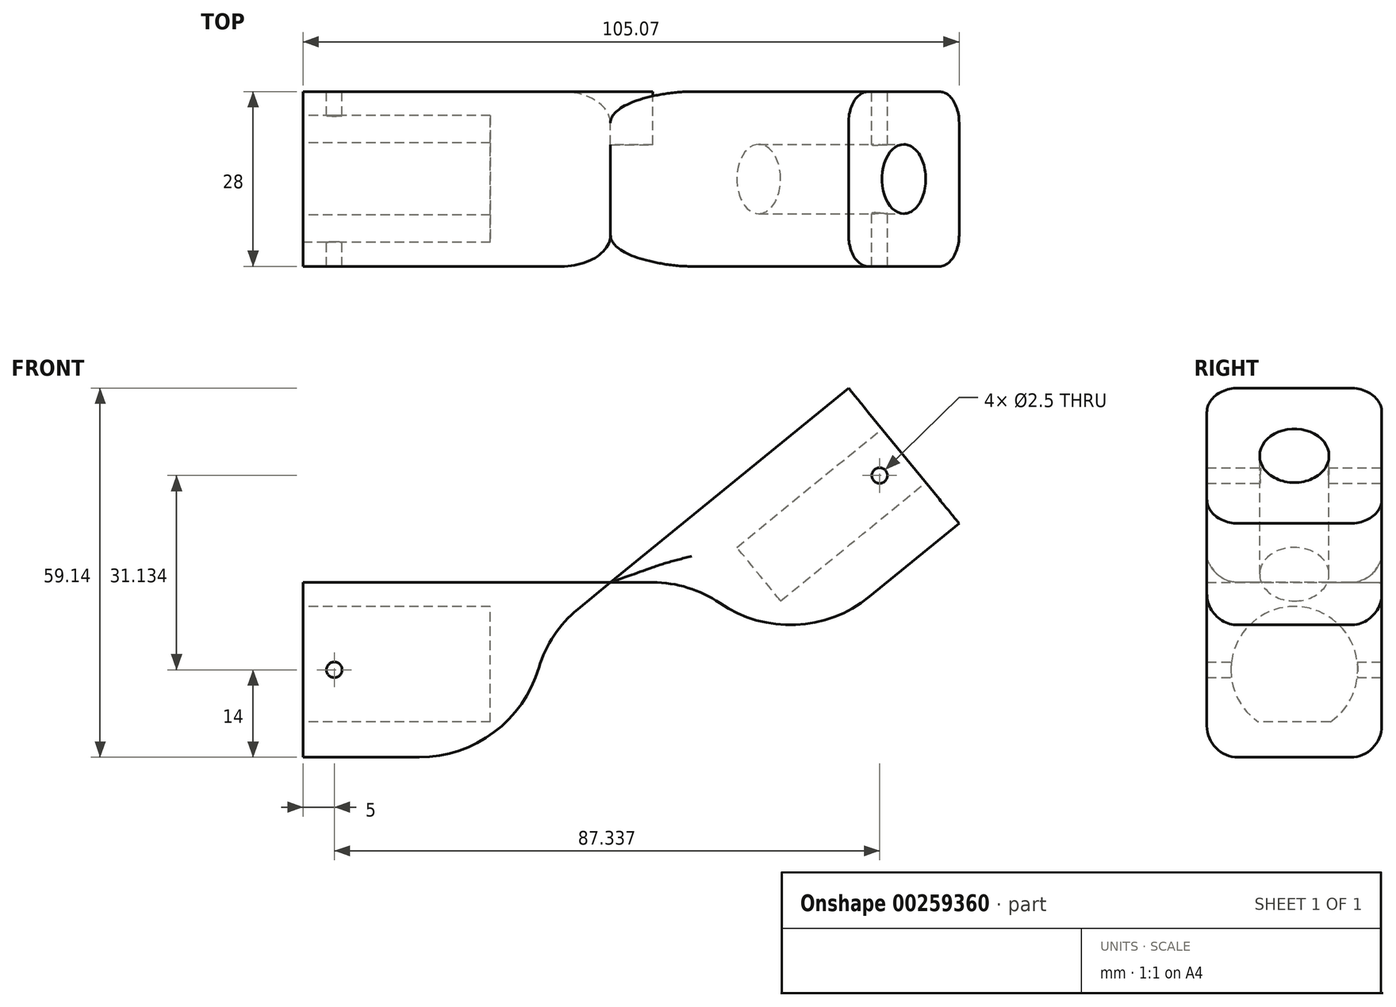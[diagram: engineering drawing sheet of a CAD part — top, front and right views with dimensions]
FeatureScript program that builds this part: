
annotation { "Feature Type Name" : "Feature", "Feature Type Description" : "" }
export const myFeature = defineFeature(function(context is Context, id is Id, definition is map)
    precondition{}
    {
        {
            var Q0;
            Q0=qCreatedBy(makeId("Front.planeOp"),FACE);
            var sketch = newSketch(context, id + "F0", { "sketchPlane" : qUnion([Q0])});
            skLineSegment(sketch, "E0.bottom", {"start": v(-75, 28) * mm, "end": v(-19, 28) * mm});
            skLineSegment(sketch, "E0.top", {"start": v(-75, 0) * mm, "end": v(-35.73, 0) * mm});
            skLineSegment(sketch, "E0.left", {"start": v(-75, 28) * mm, "end": v(-75, 0) * mm});
            skCircle(sketch, "E1", {"center": v(-19, 9) * mm, "radius": 19 * mm});
            skPoint(sketch, "E2.orphan", {"position": v(0, 0) * mm});
            skSolve(sketch);
        }
        {
            var Q0;
            Q0 = qSketchRegion(id + "F0", true);
            extrude(context, id + "F1", {"entities" : qUnion([Q0]), "endBound" : BoundingType.SYMMETRIC, "depth" : 28 * mm});
        }
        {
            var Q0;
            Q0=qCreatedBy(makeId("Front.planeOp"),FACE);
            var sketch = newSketch(context, id + "F2", { "sketchPlane" : qUnion([Q0])});
            skArc(sketch, "E3", {"start": v(-31.02, 23.72) * mm, "mid": v(-25.47, -8.87) * mm, "end": v(-0.35, 12.61) * mm});
            skLineSegment(sketch, "E4", {"start": v(-0.35, 12.61) * mm, "end": v(30.07, 37.45) * mm});
            skLineSegment(sketch, "E5", {"start": v(30.07, 37.45) * mm, "end": v(12.35, 59.14) * mm});
            skLineSegment(sketch, "E6", {"start": v(12.35, 59.14) * mm, "end": v(-31.02, 23.72) * mm});
            skSolve(sketch);
        }
        {
            var Q0;
            Q0 = qSketchRegion(id + "F2", true);
            extrude(context, id + "F3", {"entities" : qUnion([Q0]), "endBound" : BoundingType.SYMMETRIC, "depth" : 28 * mm});
        }
        {
            var Q0;
            Q0=makeQuery(id+"F3.opExtrude","CAP_FACE",FACE,{"disambiguationData":[OSD([sQuery(id+"F2.wireOp",EDGE,"E3"),sQuery(id+"F2.wireOp",EDGE,"E4"),sQuery(id+"F2.wireOp",EDGE,"E5"),sQuery(id+"F2.wireOp",EDGE,"E6")])],"isStart":false});
            var sketch = newSketch(context, id + "F4", { "sketchPlane" : qUnion([Q0])});
            skCircle(sketch, "E7", {"center": v(-19, 9) * mm, "radius": 19 * mm});
            skLineSegment(sketch, "E8", {"start": v(-31.02, 23.72) * mm, "end": v(-25.77, 28) * mm});
            skLineSegment(sketch, "E9", {"start": v(-25.77, 28) * mm, "end": v(-19, 28) * mm});
            skSolve(sketch);
        }
        {
            var Q0;
            Q0 = qSketchRegion(id + "F4", true);
            extrude(context, id + "F5", {"entities" : qUnion([Q0]), "operationType" : NewBodyOperationType.REMOVE, "oppositeDirection" : true, "depth" : 8.6 * mm});
        }
        {
            var Q0;
            Q0=makeQuery(id+"F3.opExtrude","CAP_FACE",FACE,{"disambiguationData":[OSD([sQuery(id+"F2.wireOp",EDGE,"E3"),sQuery(id+"F2.wireOp",EDGE,"E4"),sQuery(id+"F2.wireOp",EDGE,"E5"),sQuery(id+"F2.wireOp",EDGE,"E6")])],"isStart":true});
            var sketch = newSketch(context, id + "F6", { "sketchPlane" : qUnion([Q0])});
            skCircle(sketch, "E10", {"center": v(19, 9) * mm, "radius": 19 * mm});
            skLineSegment(sketch, "E11", {"start": v(31.02, 23.72) * mm, "end": v(25.79, 27.99) * mm});
            skLineSegment(sketch, "E12", {"start": v(25.79, 27.99) * mm, "end": v(19.03, 28) * mm});
            skSolve(sketch);
        }
        {
            var Q0;
            Q0 = qSketchRegion(id + "F6", true);
            extrude(context, id + "F7", {"entities" : qUnion([Q0]), "operationType" : NewBodyOperationType.REMOVE, "oppositeDirection" : true, "depth" : 8.6 * mm});
        }
        {
            var Q0;
            Q0=qCreatedBy(makeId("Front.planeOp"),FACE);
            var sketch = newSketch(context, id + "F8", { "sketchPlane" : qUnion([Q0])});
            skCircle(sketch, "E13", {"center": v(-19, 9) * mm, "radius": 19 * mm});
            skLineSegment(sketch, "E14", {"start": v(-19, 28) * mm, "end": v(-25.77, 28) * mm});
            skLineSegment(sketch, "E15", {"start": v(-25.77, 28) * mm, "end": v(-30.99, 23.74) * mm});
            skSolve(sketch);
        }
        {
            var Q0;
            Q0 = qSketchRegion(id + "F8", true);
            extrude(context, id + "F9", {"entities" : qUnion([Q0]), "operationType" : NewBodyOperationType.REMOVE, "endBound" : BoundingType.SYMMETRIC, "oppositeDirection" : true, "depth" : 11 * mm});
        }
        {
            var Q0;
            Q0=qCreatedBy(makeId("Front.planeOp"),FACE);
            var sketch = newSketch(context, id + "F10", { "sketchPlane" : qUnion([Q0])});
            skCircle(sketch, "E16", {"center": v(-19, 9) * mm, "radius": 2.25 * mm});
            skSolve(sketch);
        }
        {
            var Q0;
            Q0 = qSketchRegion(id + "F10", true);
            extrude(context, id + "F11", {"entities" : qUnion([Q0]), "operationType" : NewBodyOperationType.REMOVE, "depth" : 25 * mm, "hasSecondDirection" : true, "secondDirectionOppositeDirection" : true, "secondDirectionDepth" : 25 * mm});
        }
        {
            var Q0;
            Q0=makeQuery(id+"F1.opExtrude","SWEPT_FACE",FACE,{"disambiguationData":[OSD([sQuery(id+"F0.wireOp",EDGE,"E0.left")])]});
            var sketch = newSketch(context, id + "F12", { "sketchPlane" : qUnion([Q0])});
            skArc(sketch, "E17", {"start": v(5.77, 5.65) * mm, "mid": v(0, 24.15) * mm, "end": v(-5.77, 5.65) * mm});
            skLineSegment(sketch, "E18", {"start": v(-5.77, 5.65) * mm, "end": v(5.77, 5.65) * mm});
            skLineSegment(sketch, "E19", {"start": v(-23.71, 24.15) * mm, "end": v(30.99, 24.15) * mm, "construction": true});
            skSolve(sketch);
        }
        {
            var Q0;
            Q0 = qSketchRegion(id + "F12", true);
            extrude(context, id + "F13", {"entities" : qUnion([Q0]), "operationType" : NewBodyOperationType.REMOVE, "oppositeDirection" : true, "depth" : 30 * mm});
        }
        {
            var Q0;
            Q0=makeQuery(id+"F3.opExtrude","SWEPT_FACE",FACE,{"disambiguationData":[OSD([sQuery(id+"F2.wireOp",EDGE,"E5")])]});
            var sketch = newSketch(context, id + "F14", { "sketchPlane" : qUnion([Q0])});
            skCircle(sketch, "E20", {"center": v(0, 23.99) * mm, "radius": 5.55 * mm});
            skSolve(sketch);
        }
        {
            var Q0;
            Q0 = qSketchRegion(id + "F14", true);
            extrude(context, id + "F15", {"entities" : qUnion([Q0]), "operationType" : NewBodyOperationType.REMOVE, "oppositeDirection" : true, "depth" : 30 * mm});
        }
        {
            var Q0;
            Q0=makeQuery(id+"F3.opExtrude","CAP_FACE",FACE,{"disambiguationData":[OSD([sQuery(id+"F2.wireOp",EDGE,"E3"),sQuery(id+"F2.wireOp",EDGE,"E4"),sQuery(id+"F2.wireOp",EDGE,"E5"),sQuery(id+"F2.wireOp",EDGE,"E6")])],"isStart":true});
            var sketch = newSketch(context, id + "F16", { "sketchPlane" : qUnion([Q0])});
            skCircle(sketch, "E21", {"center": v(-17.34, 45.13) * mm, "radius": 1.25 * mm});
            skSolve(sketch);
        }
        {
            var Q0;
            Q0 = qSketchRegion(id + "F16", true);
            extrude(context, id + "F17", {"entities" : qUnion([Q0]), "operationType" : NewBodyOperationType.REMOVE, "oppositeDirection" : true, "depth" : 33.3 * mm});
        }
        {
            var Q0;
            Q0=makeQuery(id+"F1.opExtrude","CAP_FACE",FACE,{"disambiguationData":[OSD([sQuery(id+"F0.wireOp",EDGE,"E0.bottom"),sQuery(id+"F0.wireOp",EDGE,"E0.top"),sQuery(id+"F0.wireOp",EDGE,"E0.left"),sQuery(id+"F0.wireOp",EDGE,"E1")])],"isStart":true});
            var sketch = newSketch(context, id + "F18", { "sketchPlane" : qUnion([Q0])});
            skCircle(sketch, "E22", {"center": v(70, 14) * mm, "radius": 1.25 * mm});
            skSolve(sketch);
        }
        {
            var Q0;
            Q0 = qSketchRegion(id + "F18", true);
            extrude(context, id + "F19", {"entities" : qUnion([Q0]), "operationType" : NewBodyOperationType.REMOVE, "oppositeDirection" : true, "depth" : 35.3 * mm});
        }
        {
            var Q0;
            {var subQ0=sQuery(id+"F8.wireOp",EDGE,"E13");var subQ1=sQuery(id+"F0.wireOp",EDGE,"E1");var subQ2=sQuery(id+"F0.wireOp",EDGE,"E0.top");Q0=makeQuery(id+"F9.boolean.opBoolean","SPLIT",EDGE,{"disambiguationData":[TD([makeQuery(id+"F1.opExtrude","CAP_FACE",FACE,{"disambiguationData":[OSD([sQuery(id+"F0.wireOp",EDGE,"E0.bottom"),subQ2,sQuery(id+"F0.wireOp",EDGE,"E0.left"),subQ1])],"isStart":false}),makeQuery(id+"F1.opExtrude","SWEPT_FACE",FACE,{"disambiguationData":[OSD([subQ2])]}),makeQuery(id+"F1.opExtrude","SWEPT_FACE",FACE,{"disambiguationData":[OSD([subQ1])]}),makeQuery(id+"F9.opExtrude","SWEPT_FACE",FACE,{"disambiguationData":[OSD([subQ0])]}),makeQuery(id+"F9.opExtrude","CAP_FACE",FACE,{"disambiguationData":[OSD([subQ0,sQuery(id+"F8.wireOp",EDGE,"E14"),sQuery(id+"F8.wireOp",EDGE,"E15")])],"isStart":true})])],"derivedFrom":makeQuery(id+"F1.opExtrude","SWEPT_EDGE",EDGE,{"disambiguationData":[OSD([subQ2,subQ1])]})});}
            var Q1;
            {var subQ0=sQuery(id+"F8.wireOp",EDGE,"E13");var subQ1=sQuery(id+"F0.wireOp",EDGE,"E1");var subQ2=sQuery(id+"F0.wireOp",EDGE,"E0.top");Q1=makeQuery(id+"F9.boolean.opBoolean","SPLIT",EDGE,{"disambiguationData":[TD([makeQuery(id+"F1.opExtrude","CAP_FACE",FACE,{"disambiguationData":[OSD([sQuery(id+"F0.wireOp",EDGE,"E0.bottom"),subQ2,sQuery(id+"F0.wireOp",EDGE,"E0.left"),subQ1])],"isStart":true}),makeQuery(id+"F1.opExtrude","SWEPT_FACE",FACE,{"disambiguationData":[OSD([subQ2])]}),makeQuery(id+"F1.opExtrude","SWEPT_FACE",FACE,{"disambiguationData":[OSD([subQ1])]}),makeQuery(id+"F9.opExtrude","SWEPT_FACE",FACE,{"disambiguationData":[OSD([subQ0])]}),makeQuery(id+"F9.opExtrude","CAP_FACE",FACE,{"disambiguationData":[OSD([subQ0,sQuery(id+"F8.wireOp",EDGE,"E14"),sQuery(id+"F8.wireOp",EDGE,"E15")])],"isStart":false})])],"derivedFrom":makeQuery(id+"F1.opExtrude","SWEPT_EDGE",EDGE,{"disambiguationData":[OSD([subQ2,subQ1])]})});}
            var Q2;
            {var subQ0=sQuery(id+"F4.wireOp",EDGE,"E7");var subQ2=makeQuery(id+"F5.opExtrude","SWEPT_FACE",FACE,{"disambiguationData":[OSD([subQ0])]});var subQ3=sQuery(id+"F2.wireOp",EDGE,"E4");var subQ5=sQuery(id+"F2.wireOp",EDGE,"E3");Q2=makeQuery(id+"F7.boolean.opBoolean","SPLIT",EDGE,{"disambiguationData":[TD([makeQuery(id+"F5.boolean.opBoolean","COPY",FACE,{"derivedFrom":subQ2})])],"derivedFrom":makeQuery(id+"F5.boolean.opBoolean","SPLIT",EDGE,{"disambiguationData":[TD([makeQuery(id+"F3.opExtrude","CAP_FACE",FACE,{"disambiguationData":[OSD([subQ5,subQ3,sQuery(id+"F2.wireOp",EDGE,"E5"),sQuery(id+"F2.wireOp",EDGE,"E6")])],"isStart":true})])],"derivedFrom":makeQuery(id+"F3.opExtrude","SWEPT_EDGE",EDGE,{"disambiguationData":[OSD([subQ5,subQ3])]})})});}
            fillet(context, id + "F20", {"entities" : qUnion([Q0, Q1, Q2]), "radius" : 20 * mm, "tangentPropagation" : true, "allowEdgeOverflow" : false});
        }
        {
            var Q0;
            Q0=makeQuery(id+"F1.opExtrude","CAP_EDGE",EDGE,{"disambiguationData":[OSD([sQuery(id+"F0.wireOp",EDGE,"E0.top")])],"isStart":false});
            var Q1;
            Q1=makeQuery(id+"F1.opExtrude","CAP_EDGE",EDGE,{"disambiguationData":[OSD([sQuery(id+"F0.wireOp",EDGE,"E0.top")])],"isStart":true});
            var Q2;
            Q2=makeQuery(id+"F3.opExtrude","CAP_EDGE",EDGE,{"disambiguationData":[OSD([sQuery(id+"F2.wireOp",EDGE,"E4")])],"isStart":true});
            var Q3;
            Q3=makeQuery(id+"F3.opExtrude","CAP_EDGE",EDGE,{"disambiguationData":[OSD([sQuery(id+"F2.wireOp",EDGE,"E4")])],"isStart":false});
            var Q4;
            Q4=makeQuery(id+"F3.opExtrude","CAP_EDGE",EDGE,{"disambiguationData":[OSD([sQuery(id+"F2.wireOp",EDGE,"E6")])],"isStart":false});
            var Q5;
            Q5=makeQuery(id+"F3.opExtrude","CAP_EDGE",EDGE,{"disambiguationData":[OSD([sQuery(id+"F2.wireOp",EDGE,"E6")])],"isStart":true});
            fillet(context, id + "F21", {"entities" : qUnion([Q0, Q1, Q2, Q3, Q4, Q5]), "radius" : 5 * mm, "tangentPropagation" : true, "allowEdgeOverflow" : false});
        }
    });
